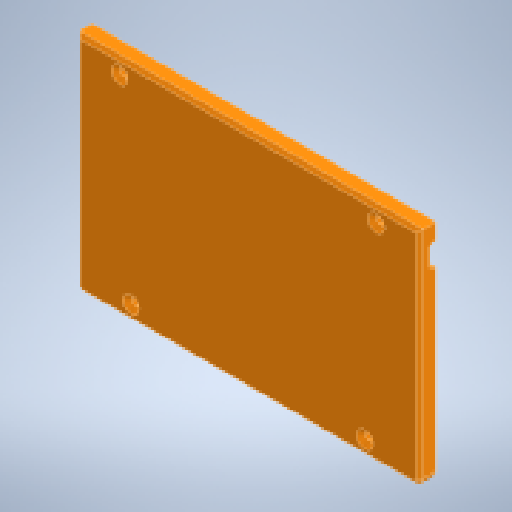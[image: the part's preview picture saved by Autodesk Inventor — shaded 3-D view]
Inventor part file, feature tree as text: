
AUTODESK INVENTOR PART (.ipt)
format: ipt  version: 2024.1 (Build 281209000, 209)  size: 331,264 bytes
history: native  units: in
note: dims shown in document units (in); Inventor stores cm internally (conversion verified against a paired STEP export)
features: extrude x7, sketch x7, fillet x3, chamfer x2
ambient origin geometry x8: Origin, YZ Plane, XZ Plane, XY Plane, X Axis, Y Axis, Z Axis, Center Point
bodies: Solid1 (feature_tree)
feature tree (19):
  extrude  "Extrusion1"  Depth=3.8287in
  extrude  "Extrusion2"  Depth=0.0984in
  extrude  "Extrusion3"  Depth=0.0984in
  extrude  "Extrusion4"  Depth=0.1969in TaperAngle=0.0deg
  fillet  "Fillet1"  Radius=0.315in
  extrude  "Extrusion5"  Depth=0.315in
  fillet  "Fillet2"  Radius=0.7874in
  extrude  "Extrusion6"  Depth=0.315in
  fillet  "Fillet3"  Radius=0.315in
  chamfer  "Chamfer1"  Distance=0.315in
  extrude  "Extrusion7"  Depth=0.5906in
  chamfer  "Chamfer2"  Distance=0.5906in
  sketch  "Sketch1"  dims[d0=5.9055in d1=3.8287in]
  sketch  "Sketch2"  dims[d2=0.2756in d3=0.0in d4=0.0984in]
  sketch  "Sketch3"  dims[d5=0.0984in d6=0.0984in]
  sketch  "Sketch4"  dims[d7=0.0984in d8=0.1969in d9=0.0in d10=0.315in]
  sketch  "Sketch5"  dims[d11=0.315in d12=0.315in d13=0.7874in]
  sketch  "Sketch6"  dims[d14=0.7874in d15=0.315in d16=0.315in]
  sketch  "Sketch7"  dims[d17=0.315in d18=0.315in d19=0.5906in d20=0.5906in d21=0.4134in d22=0.1969in d23=0.0in d24=0.126in d25=0.126in d26=0.9449in d27=0.2559in d28=0.9449in d29=0.2559in d30=0.126in d31=0.126in d32=0.748in d33=0.2559in d34=0.2559in d35=0.748in d36=0.0in d37=0.0in d38=0.1181in d39=0.1181in d40=0.2756in d41=0.3937in d42=0.0in d43=0.0in d44=0.0787in d45=0.1181in d46=0.3937in d47=0.2756in d48=0.3937in d49=0.0in d50=0.0787in d51=0.0591in d52=0.0787in d53=45.0deg d54=0.1969in d55=0.4331in d56=0.0984in d57=0.3937in d58=0.0in d59=0.0787in d60=0.0787in d61=45.0deg]
